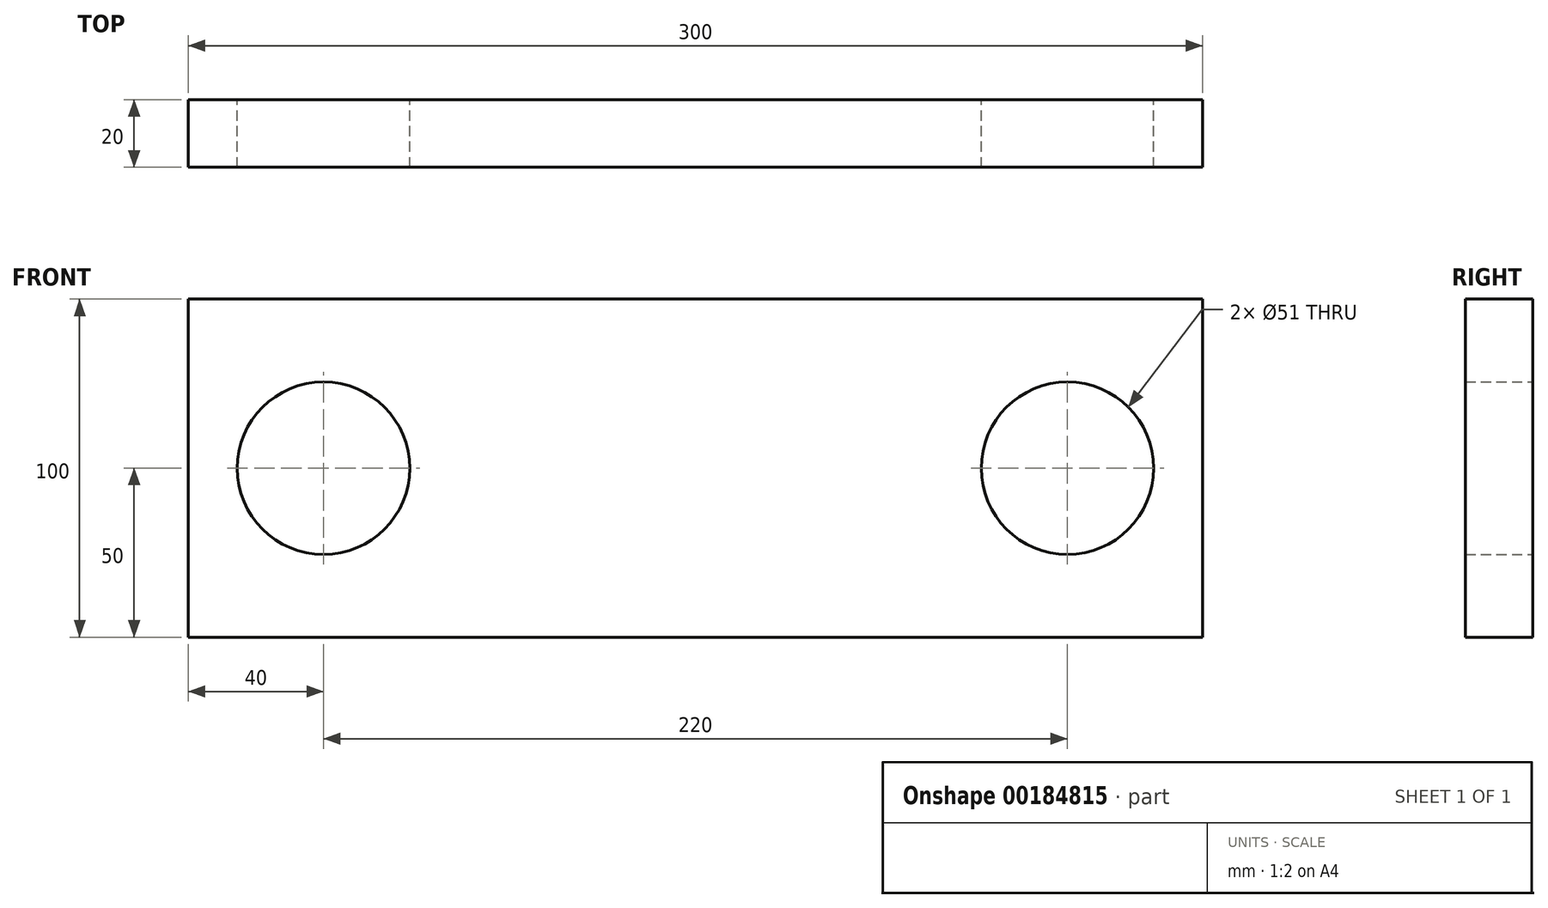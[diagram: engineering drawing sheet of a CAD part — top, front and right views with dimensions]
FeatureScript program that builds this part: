
annotation { "Feature Type Name" : "Feature", "Feature Type Description" : "" }
export const myFeature = defineFeature(function(context is Context, id is Id, definition is map)
    precondition{}
    {
        {
            var Q0;
            Q0=qCreatedBy(makeId("Front.planeOp"),FACE);
            var sketch = newSketch(context, id + "F0", { "sketchPlane" : qUnion([Q0])});
            skLineSegment(sketch, "E0.bottom", {"start": v(0, 0) * mm, "end": v(300, 0) * mm});
            skLineSegment(sketch, "E0.top", {"start": v(0, 100) * mm, "end": v(300, 100) * mm});
            skLineSegment(sketch, "E0.left", {"start": v(0, 0) * mm, "end": v(0, 100) * mm});
            skLineSegment(sketch, "E0.right", {"start": v(300, 0) * mm, "end": v(300, 100) * mm});
            skLineSegment(sketch, "E1", {"start": v(0, 50) * mm, "end": v(40, 50) * mm, "construction": true});
            skPoint(sketch, "E1.endSnap0", {"position": v(0, 50) * mm});
            skCircle(sketch, "E2", {"center": v(40, 50) * mm, "radius": 25.5 * mm});
            skLineSegment(sketch, "E3", {"start": v(300, 50) * mm, "end": v(260, 50) * mm, "construction": true});
            skCircle(sketch, "E4", {"center": v(260, 50) * mm, "radius": 25.5 * mm});
            skSolve(sketch);
        }
        {
            var Q0;
            Q0=makeQuery(id+"F0.imprint","IMPRINT",FACE,{"disambiguationData":[TD([[makeQuery(id+"F0.imprint","IMPRINT",EDGE,{"derivedFrom":sQuery(id+"F0.wireOp",EDGE,"E0.bottom")}),1.0]])]});
            extrude(context, id + "F1", {"entities" : qUnion([Q0]), "depth" : 20 * mm});
        }
    });
